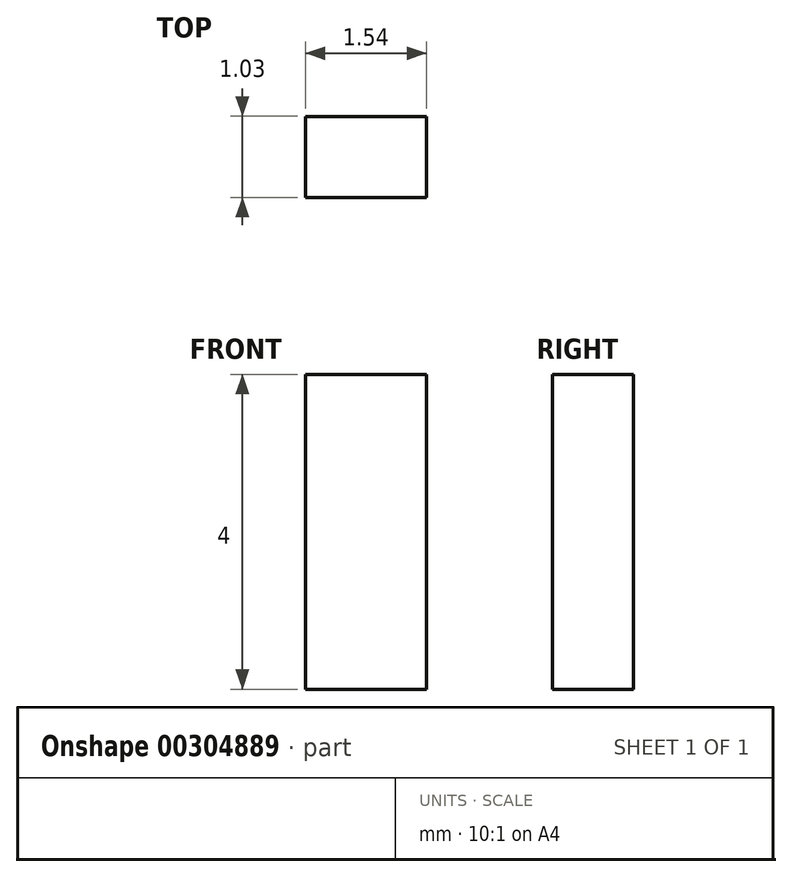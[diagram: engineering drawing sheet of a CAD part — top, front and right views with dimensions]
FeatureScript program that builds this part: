
annotation { "Feature Type Name" : "Feature", "Feature Type Description" : "" }
export const myFeature = defineFeature(function(context is Context, id is Id, definition is map)
    precondition{}
    {
        {
            var Q0;
            Q0=qCreatedBy(makeId("Top.planeOp"),FACE);
            var sketch = newSketch(context, id + "F0", { "sketchPlane" : qUnion([Q0])});
            skLineSegment(sketch, "E0.bottom", {"start": v(-40.42, -5.5) * mm, "end": v(-38.88, -5.5) * mm});
            skLineSegment(sketch, "E0.top", {"start": v(-40.42, -6.52) * mm, "end": v(-38.88, -6.52) * mm});
            skLineSegment(sketch, "E0.left", {"start": v(-40.42, -5.5) * mm, "end": v(-40.42, -6.52) * mm});
            skLineSegment(sketch, "E0.right", {"start": v(-38.88, -5.5) * mm, "end": v(-38.88, -6.52) * mm});
            skSolve(sketch);
        }
        {
            var Q0;
            Q0=makeQuery(id+"F0.imprint","IMPRINT",FACE,{"disambiguationData":[TD([[makeQuery(id+"F0.imprint","IMPRINT",EDGE,{"derivedFrom":sQuery(id+"F0.wireOp",EDGE,"E0.bottom")}),-1.0]])]});
            extrude(context, id + "F1", {"entities" : qUnion([Q0]), "depth" : 4 * mm});
        }
    });
